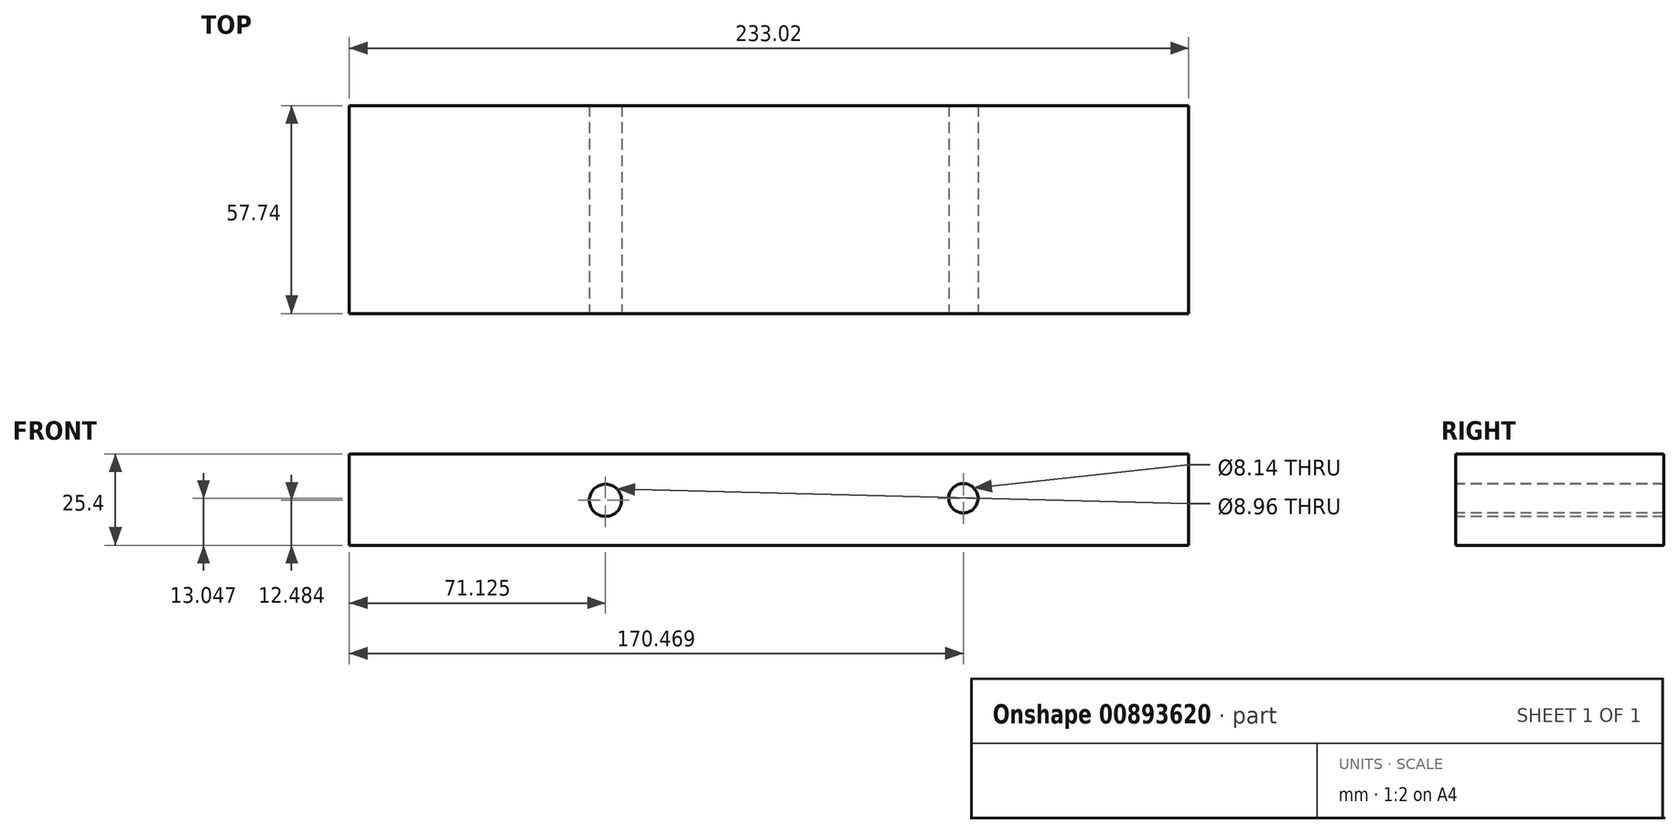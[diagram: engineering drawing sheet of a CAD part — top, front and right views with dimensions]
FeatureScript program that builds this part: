
annotation { "Feature Type Name" : "Feature", "Feature Type Description" : "" }
export const myFeature = defineFeature(function(context is Context, id is Id, definition is map)
    precondition{}
    {
        {
            var Q0;
            Q0=qCreatedBy(makeId("Top.planeOp"),FACE);
            var sketch = newSketch(context, id + "F0", { "sketchPlane" : qUnion([Q0])});
            skPoint(sketch, "E0.middle", {"position": v(0, 0) * mm});
            skLineSegment(sketch, "E1.bottom", {"start": v(116.5, -28.87) * mm, "end": v(-116.5, -28.87) * mm});
            skLineSegment(sketch, "E1.top", {"start": v(116.5, 28.87) * mm, "end": v(-116.5, 28.87) * mm});
            skLineSegment(sketch, "E1.left", {"start": v(116.5, -28.87) * mm, "end": v(116.5, 28.87) * mm});
            skLineSegment(sketch, "E1.right", {"start": v(-116.5, -28.87) * mm, "end": v(-116.5, 28.87) * mm});
            skSolve(sketch);
        }
        {
            var Q0;
            Q0=makeQuery(id+"F0.imprint","IMPRINT",FACE,{"disambiguationData":[TD([[makeQuery(id+"F0.imprint","IMPRINT",EDGE,{"derivedFrom":sQuery(id+"F0.wireOp",EDGE,"E1.bottom")}),-1.0]])]});
            extrude(context, id + "F1", {"entities" : qUnion([Q0]), "depth" : 25.4 * mm, "offsetDistance" : 25.4 * mm});
        }
        {
            var Q0;
            Q0=makeQuery(id+"F1.opExtrude","SWEPT_FACE",FACE,{"disambiguationData":[OSD([sQuery(id+"F0.wireOp",EDGE,"E1.bottom")])]});
            var sketch = newSketch(context, id + "F2", { "sketchPlane" : qUnion([Q0])});
            skCircle(sketch, "E2", {"center": v(-45.39, 12.48) * mm, "radius": 4.48 * mm});
            skCircle(sketch, "E3", {"center": v(53.96, 13.05) * mm, "radius": 4.07 * mm});
            skSolve(sketch);
        }
        {
            var Q0;
            Q0 = qSketchRegion(id + "F2", true);
            extrude(context, id + "F3", {"entities" : qUnion([Q0]), "operationType" : NewBodyOperationType.REMOVE, "endBound" : BoundingType.THROUGH_ALL, "oppositeDirection" : true, "depth" : 25.4 * mm, "offsetDistance" : 25.4 * mm});
        }
    });
